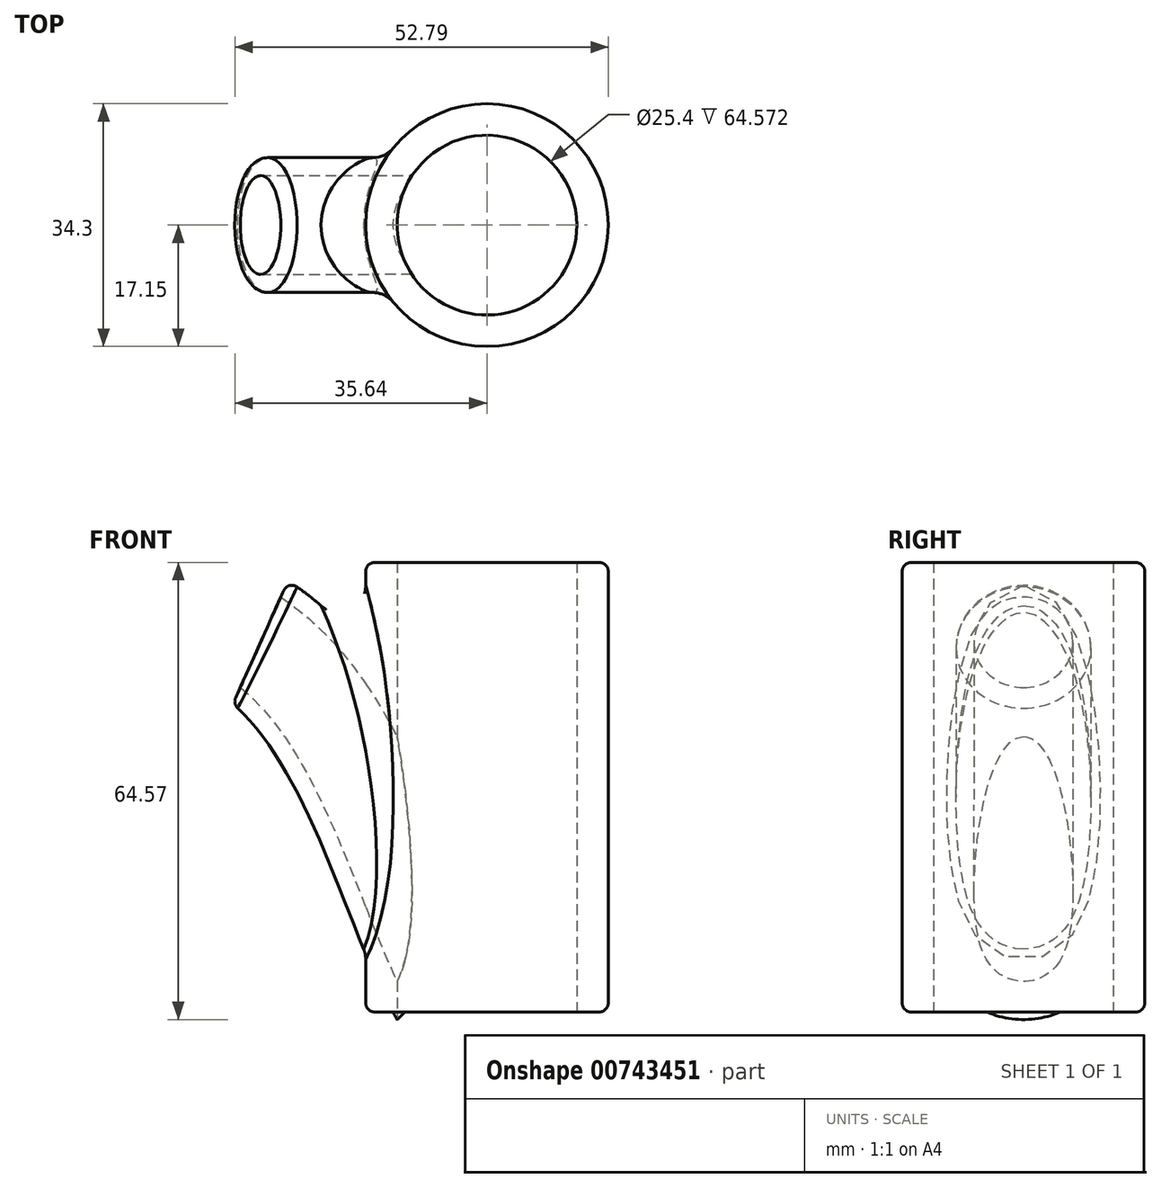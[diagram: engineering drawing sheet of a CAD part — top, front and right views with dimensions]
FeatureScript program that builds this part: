
annotation { "Feature Type Name" : "Feature", "Feature Type Description" : "" }
export const myFeature = defineFeature(function(context is Context, id is Id, definition is map)
    precondition{}
    {
        {
            var Q0;
            Q0=qCreatedBy(makeId("Top.planeOp"),FACE);
            var sketch = newSketch(context, id + "F0", { "sketchPlane" : qUnion([Q0])});
            skCircle(sketch, "E0", {"center": v(0, 0) * mm, "radius": 12.7 * mm});
            skCircle(sketch, "E1", {"center": v(0, 0) * mm, "radius": 17.15 * mm});
            skSolve(sketch);
        }
        {
            var Q0;
            Q0=makeQuery(id+"F0.imprint","IMPRINT",FACE,{"disambiguationData":[TD([[makeQuery(id+"F0.imprint","IMPRINT",EDGE,{"derivedFrom":sQuery(id+"F0.wireOp",EDGE,"E0")}),-1.0]])]});
            extrude(context, id + "F1", {"entities" : qUnion([Q0]), "depth" : 63.5 * mm, "offsetDistance" : 25.4 * mm});
        }
        {
            var Q0;
            Q0=qCreatedBy(makeId("Right.planeOp"),FACE);
            cPlane(context, id + "F2", {"entities" : qUnion([Q0]), "cplaneType" : CPlaneType.OFFSET, "offset" : 16.76 * mm, "oppositeDirection" : true, "width" : 152.4 * mm, "height" : 152.4 * mm});
        }
        {
            var Q0;
            Q0=qCreatedBy(id+"F2.planeOp",FACE);
            var sketch = newSketch(context, id + "F3", { "sketchPlane" : qUnion([Q0])});
            skLineSegment(sketch, "E2", {"start": v(45.22, 63.3) * mm, "end": v(-44.35, 63.3) * mm});
            skSolve(sketch);
        }
        {
            var Q0;
            Q0=sQuery(id+"F3.wireOp",EDGE,"E2");
            cPlane(context, id + "F4", {"entities" : qUnion([Q0]), "cplaneType" : CPlaneType.LINE_ANGLE, "offset" : 25.4 * mm, "angle" : 55 * degree, "width" : 152.4 * mm, "height" : 152.4 * mm});
        }
        {
            var Q0;
            Q0=qCreatedBy(id+"F4.planeOp",FACE);
            var sketch = newSketch(context, id + "F5", { "sketchPlane" : qUnion([Q0])});
            skCircle(sketch, "E3", {"center": v(0, 23.75) * mm, "radius": 6.99 * mm});
            skCircle(sketch, "E4", {"center": v(0, 23.75) * mm, "radius": 9.53 * mm});
            skSolve(sketch);
        }
        {
            var Q0;
            {var subQ0=sQuery(id+"F5.wireOp",EDGE,"E4");Q0=makeQuery(id+"FPSWW7IS3d8COEw_1.boolean.opBoolean","SPLIT",FACE,{"disambiguationData":[TD([makeQuery(id+"F1.opExtrude","SWEPT_FACE",FACE,{"disambiguationData":[OSD([sQuery(id+"F0.wireOp",EDGE,"E1")])]})])],"derivedFrom":makeQuery(id+"FPSWW7IS3d8COEw_1.opExtrude","SWEPT_FACE",FACE,{"disambiguationData":[OSD([subQ0])]})});}
            var Q1;
            Q1=makeQuery(id+"F1.opExtrude","CAP_EDGE",EDGE,{"disambiguationData":[OSD([sQuery(id+"F0.wireOp",EDGE,"E1")])],"isStart":false});
            var Q2;
            Q2=makeQuery(id+"F1.opExtrude","CAP_EDGE",EDGE,{"disambiguationData":[OSD([sQuery(id+"F0.wireOp",EDGE,"E1")])],"isStart":true});
            fillet(context, id + "F6", {"entities" : qUnion([Q0, Q1, Q2]), "radius" : 1.27 * mm, "tangentPropagation" : true, "allowEdgeOverflow" : false});
        }
        {
            var Q0;
            Q0=makeQuery(id+"F1.opExtrude","CAP_FACE",FACE,{"disambiguationData":[OSD([sQuery(id+"F0.wireOp",EDGE,"E0"),sQuery(id+"F0.wireOp",EDGE,"E1")])],"isStart":true});
            var sketch = newSketch(context, id + "F7", { "sketchPlane" : qUnion([Q0])});
            skCircle(sketch, "E5", {"center": v(0, 0) * mm, "radius": 12.7 * mm});
            skSolve(sketch);
        }
        {
            var Q0;
            Q0=qSketchRegion(id+"F7",true);
            extrude(context, id + "F8", {"entities" : qUnion([Q0]), "operationType" : NewBodyOperationType.REMOVE, "oppositeDirection" : true, "depth" : 68.07 * mm, "offsetDistance" : 25.4 * mm});
        }
        {
            var Q0;
            Q0=qCreatedBy(makeId("Front.planeOp"),FACE);
            var sketch = newSketch(context, id + "F9", { "sketchPlane" : qUnion([Q0])});
            skPoint(sketch, "E6", {"position": v(-31.9, 52.7) * mm});
            skFitSpline(sketch, "E7", {"points": [v(-32.02, 52.18) * mm, v(-2.01, 0) * mm], "startDerivative": vector(50.82, -36.2) * mm, "endDerivative": vector(26.13, -28.64) * mm});
            skSolve(sketch);
        }
        {
            var Q0;
            Q0=makeQuery(id+"F5.imprint","IMPRINT",FACE,{"disambiguationData":[TD([[makeQuery(id+"F5.imprint","IMPRINT",EDGE,{"derivedFrom":sQuery(id+"F5.wireOp",EDGE,"E3")}),-1.0]])]});
            var Q1;
            Q1=sQuery(id+"F9.wireOp",EDGE,"E7");
            sweep(context, id + "F10", {"operationType" : NewBodyOperationType.ADD, "profiles" : qUnion([Q0]), "path" : qUnion([Q1])});
        }
        {
            var Q0;
            Q0=makeQuery(id+"F1.opExtrude","CAP_FACE",FACE,{"disambiguationData":[OSD([sQuery(id+"F0.wireOp",EDGE,"E0"),sQuery(id+"F0.wireOp",EDGE,"E1")])],"isStart":true});
            var sketch = newSketch(context, id + "F11", { "sketchPlane" : qUnion([Q0])});
            skCircle(sketch, "E8", {"center": v(0, 0) * mm, "radius": 12.7 * mm});
            skSolve(sketch);
        }
        {
            var Q0;
            Q0=qSketchRegion(id+"F11",true);
            extrude(context, id + "F12", {"entities" : qUnion([Q0]), "operationType" : NewBodyOperationType.REMOVE, "oppositeDirection" : true, "depth" : 47.75 * mm, "offsetDistance" : 25.4 * mm, "hasSecondDirection" : true, "secondDirectionOppositeDirection" : false, "secondDirectionDepth" : 25.4 * mm});
        }
        {
            var Q0;
            Q0=makeQuery(id+"F10.boolean.opBoolean","INTERSECT",EDGE,{"derivedFrom":[makeQuery(id+"F1.opExtrude","SWEPT_FACE",FACE,{"disambiguationData":[OSD([sQuery(id+"F0.wireOp",EDGE,"E1")])]}),makeQuery(id+"F10.opSweep","SWEPT_FACE",FACE,{"disambiguationData":[OSD([sQuery(id+"F5.wireOp",EDGE,"E4"),sQuery(id+"F9.wireOp",EDGE,"E7")])]})]});
            fillet(context, id + "F13", {"entities" : qUnion([Q0]), "radius" : 3.8 * mm, "tangentPropagation" : true, "allowEdgeOverflow" : false});
        }
        {
            var Q0;
            Q0=makeQuery(id+"F10.opSweep","CAP_FACE",FACE,{"disambiguationData":[OSD([sQuery(id+"F5.wireOp",EDGE,"E3"),sQuery(id+"F5.wireOp",EDGE,"E4"),sQuery(id+"F9.wireOp",VERTEX,"E7.start")])],"isStart":true});
            var sketch = newSketch(context, id + "F14", { "sketchPlane" : qUnion([Q0])});
            skCircle(sketch, "E9", {"center": v(0, 34.54) * mm, "radius": 6.99 * mm});
            skSolve(sketch);
        }
        {
            var Q0;
            Q0=makeQuery(id+"F14.imprint","IMPRINT",FACE,{"disambiguationData":[TD([[makeQuery(id+"F14.imprint","IMPRINT",EDGE,{"derivedFrom":sQuery(id+"F14.wireOp",EDGE,"E9")}),-1.0]])]});
            var Q1;
            Q1=sQuery(id+"F9.wireOp",EDGE,"E7");
            sweep(context, id + "F15", {"operationType" : NewBodyOperationType.REMOVE, "profiles" : qUnion([Q0]), "path" : qUnion([Q1])});
        }
        {
            var Q0;
            Q0=makeQuery(id+"F10.opSweep","CAP_EDGE",EDGE,{"disambiguationData":[OSD([sQuery(id+"F5.wireOp",EDGE,"E4"),sQuery(id+"F9.wireOp",VERTEX,"E7.start")])],"isStart":true});
            fillet(context, id + "F16", {"entities" : qUnion([Q0]), "radius" : 1.27 * mm, "tangentPropagation" : true, "allowEdgeOverflow" : false});
        }
    });
